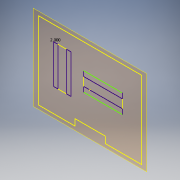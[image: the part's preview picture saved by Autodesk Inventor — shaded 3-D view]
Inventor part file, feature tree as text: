
AUTODESK INVENTOR PART (.ipt)
format: ipt  version: 2018 (Build 220112000, 112)  size: 124,928 bytes
history: native  units: in
note: dims shown in document units (in); Inventor stores cm internally (conversion verified against a paired STEP export)
features: other x3, plane x1, extrude x1, sketch x1, reference x1
ambient origin geometry x8: Origin, YZ Plane, XZ Plane, XY Plane, X Axis, Y Axis, Z Axis, Center Point
bodies: Body1 (feature_tree)
feature tree (7):
  plane  "Work Plane1"
  extrude  "Extrusion2"  Depth=0.1in TaperAngle=0.0deg
  sketch  "Sketch3"  dims[d4=2.0in d5=0.1in d6=0.0in]
  reference  "Reference2"
  other  "<userpath> Alt\Documents\PowerPREP\PowerPREPField.iam"
  other  "PowerPREPField.iam"
  other  "Plywood:1"
